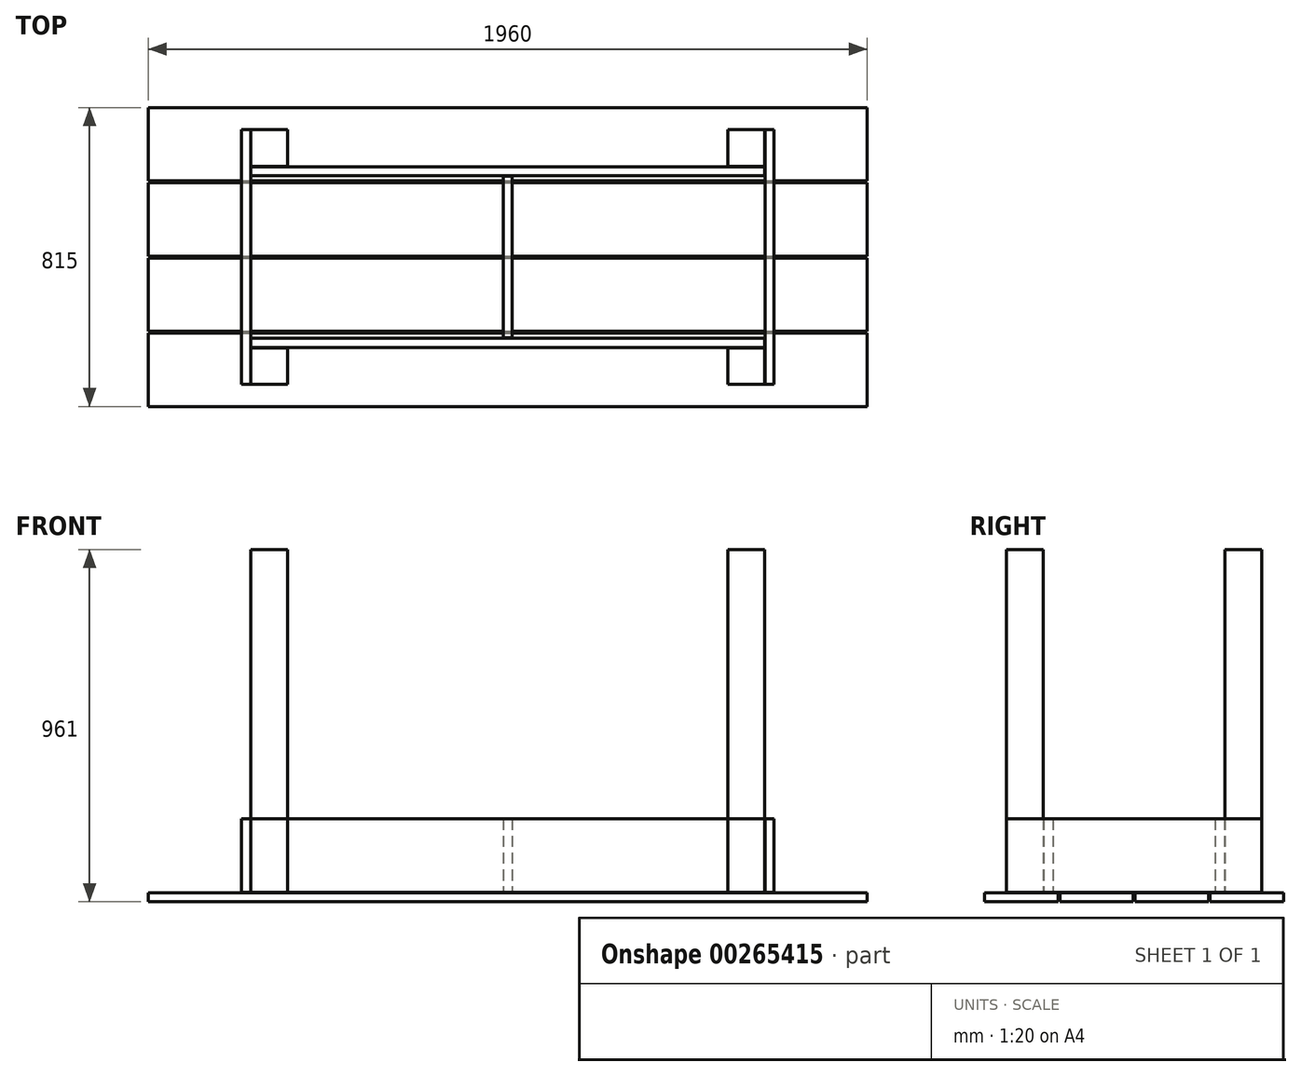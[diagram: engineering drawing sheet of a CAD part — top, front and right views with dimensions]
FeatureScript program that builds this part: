
annotation { "Feature Type Name" : "Feature", "Feature Type Description" : "" }
export const myFeature = defineFeature(function(context is Context, id is Id, definition is map)
    precondition{}
    {
        {
            var Q0;
            Q0=qCreatedBy(makeId("Top.planeOp"),FACE);
            var sketch = newSketch(context, id + "F0", { "sketchPlane" : qUnion([Q0])});
            skLineSegment(sketch, "E0.bottom", {"start": v(-916.06, -210.49) * mm, "end": v(1043.94, -210.49) * mm});
            skLineSegment(sketch, "E0.top", {"start": v(-916.06, -410.49) * mm, "end": v(1043.94, -410.49) * mm});
            skLineSegment(sketch, "E0.left", {"start": v(-916.06, -210.49) * mm, "end": v(-916.06, -410.49) * mm});
            skLineSegment(sketch, "E0.right", {"start": v(1043.94, -210.49) * mm, "end": v(1043.94, -410.49) * mm});
            skLineSegment(sketch, "E1.0.1.0", {"start": v(-916.06, -5.49) * mm, "end": v(-916.06, -205.49) * mm});
            skLineSegment(sketch, "E1.0.1.1", {"start": v(-916.06, -5.49) * mm, "end": v(1043.94, -5.49) * mm});
            skLineSegment(sketch, "E1.0.1.2", {"start": v(-916.06, -205.49) * mm, "end": v(1043.94, -205.49) * mm});
            skLineSegment(sketch, "E1.0.1.3", {"start": v(1043.94, -5.49) * mm, "end": v(1043.94, -205.49) * mm});
            skLineSegment(sketch, "E1.0.2.0", {"start": v(-916.06, 199.51) * mm, "end": v(-916.06, -0.49) * mm});
            skLineSegment(sketch, "E1.0.2.1", {"start": v(-916.06, 199.51) * mm, "end": v(1043.94, 199.51) * mm});
            skLineSegment(sketch, "E1.0.2.2", {"start": v(-916.06, -0.49) * mm, "end": v(1043.94, -0.49) * mm});
            skLineSegment(sketch, "E1.0.2.3", {"start": v(1043.94, 199.51) * mm, "end": v(1043.94, -0.49) * mm});
            skLineSegment(sketch, "E1.0.3.0", {"start": v(-916.06, 404.51) * mm, "end": v(-916.06, 204.51) * mm});
            skLineSegment(sketch, "E1.0.3.1", {"start": v(-916.06, 404.51) * mm, "end": v(1043.94, 404.51) * mm});
            skLineSegment(sketch, "E1.0.3.2", {"start": v(-916.06, 204.51) * mm, "end": v(1043.94, 204.51) * mm});
            skLineSegment(sketch, "E1.0.3.3", {"start": v(1043.94, 404.51) * mm, "end": v(1043.94, 204.51) * mm});
            skLineSegment(sketch, "E1.direction1", {"start": v(-916.06, -410.49) * mm, "end": v(-891.06, -410.49) * mm, "construction": true});
            skLineSegment(sketch, "E1.direction2", {"start": v(-916.06, -410.49) * mm, "end": v(-916.06, -205.49) * mm, "construction": true});
            skSolve(sketch);
        }
        {
            var Q0;
            Q0 = qSketchRegion(id + "F0", true);
            extrude(context, id + "F1", {"entities" : qUnion([Q0]), "depth" : 25 * mm});
        }
        {
            var Q0;
            Q0=makeQuery(id+"F1.opExtrude","CAP_FACE",FACE,{"disambiguationData":[OSD([sQuery(id+"F0.wireOp",EDGE,"E0.bottom"),sQuery(id+"F0.wireOp",EDGE,"E0.top"),sQuery(id+"F0.wireOp",EDGE,"E0.left"),sQuery(id+"F0.wireOp",EDGE,"E0.right")])],"isStart":false});
            cPlane(context, id + "F2", {"entities" : qUnion([Q0]), "cplaneType" : CPlaneType.OFFSET, "offset" : 1 * mm, "width" : 150 * mm, "height" : 150 * mm});
        }
        {
            var Q0;
            Q0=qCreatedBy(id+"F2.planeOp",FACE);
            var sketch = newSketch(context, id + "F3", { "sketchPlane" : qUnion([Q0])});
            skLineSegment(sketch, "E2.bottom", {"start": v(-916.06, 404.51) * mm, "end": v(1043.94, 404.51) * mm, "construction": true});
            skLineSegment(sketch, "E2.top", {"start": v(-916.06, -410.49) * mm, "end": v(1043.94, -410.49) * mm, "construction": true});
            skLineSegment(sketch, "E2.left", {"start": v(-916.06, 404.51) * mm, "end": v(-916.06, -410.49) * mm, "construction": true});
            skLineSegment(sketch, "E2.right", {"start": v(1043.94, 404.51) * mm, "end": v(1043.94, -410.49) * mm, "construction": true});
            skLineSegment(sketch, "E3", {"start": v(63.94, -410.49) * mm, "end": v(63.94, 404.51) * mm, "construction": true});
            skLineSegment(sketch, "E4", {"start": v(1043.94, -2.99) * mm, "end": v(-916.06, -2.99) * mm, "construction": true});
            skLineSegment(sketch, "E5.bottom", {"start": v(-636.06, 244.51) * mm, "end": v(-536.06, 244.51) * mm});
            skLineSegment(sketch, "E5.top", {"start": v(-636.06, 344.51) * mm, "end": v(-536.06, 344.51) * mm});
            skLineSegment(sketch, "E5.left", {"start": v(-636.06, 244.51) * mm, "end": v(-636.06, 344.51) * mm});
            skLineSegment(sketch, "E5.right", {"start": v(-536.06, 244.51) * mm, "end": v(-536.06, 344.51) * mm});
            skLineSegment(sketch, "E6.bottom", {"start": v(63.94, 218.51) * mm, "end": v(-636.06, 218.51) * mm});
            skLineSegment(sketch, "E6.top", {"start": v(63.94, 243.51) * mm, "end": v(-636.06, 243.51) * mm});
            skLineSegment(sketch, "E6.left", {"start": v(63.94, 218.51) * mm, "end": v(63.94, 243.51) * mm});
            skLineSegment(sketch, "E6.right", {"start": v(-636.06, 218.51) * mm, "end": v(-636.06, 243.51) * mm});
            skLineSegment(sketch, "E7.bottom", {"start": v(-662.06, -2.99) * mm, "end": v(-637.06, -2.99) * mm});
            skLineSegment(sketch, "E7.top", {"start": v(-662.06, 344.51) * mm, "end": v(-637.06, 344.51) * mm});
            skLineSegment(sketch, "E7.left", {"start": v(-662.06, -2.99) * mm, "end": v(-662.06, 344.51) * mm});
            skLineSegment(sketch, "E7.right", {"start": v(-637.06, -2.99) * mm, "end": v(-637.06, 344.51) * mm});
            skLineSegment(sketch, "E8.bottom", {"start": v(63.94, -2.99) * mm, "end": v(51.44, -2.99) * mm});
            skLineSegment(sketch, "E8.top", {"start": v(63.94, 217.51) * mm, "end": v(51.44, 217.51) * mm});
            skLineSegment(sketch, "E8.left", {"start": v(63.94, -2.99) * mm, "end": v(63.94, 217.51) * mm});
            skLineSegment(sketch, "E8.right", {"start": v(51.44, -2.99) * mm, "end": v(51.44, 217.51) * mm});
            skLineSegment(sketch, "E9.MirrorCS", {"start": v(763.94, 218.51) * mm, "end": v(763.94, 243.51) * mm});
            skLineSegment(sketch, "E10.MirrorCS", {"start": v(789.94, -2.99) * mm, "end": v(764.94, -2.99) * mm});
            skLineSegment(sketch, "E11.MirrorCS", {"start": v(789.94, 344.51) * mm, "end": v(764.94, 344.51) * mm});
            skLineSegment(sketch, "E12.MirrorCS", {"start": v(63.94, -2.99) * mm, "end": v(76.44, -2.99) * mm});
            skLineSegment(sketch, "E13.MirrorCS", {"start": v(63.94, 217.51) * mm, "end": v(76.44, 217.51) * mm});
            skLineSegment(sketch, "E14.MirrorCS", {"start": v(763.94, 244.51) * mm, "end": v(763.94, 344.51) * mm});
            skLineSegment(sketch, "E15.MirrorCS", {"start": v(763.94, 244.51) * mm, "end": v(663.94, 244.51) * mm});
            skLineSegment(sketch, "E16.MirrorCS", {"start": v(763.94, 344.51) * mm, "end": v(663.94, 344.51) * mm});
            skLineSegment(sketch, "E17.MirrorCS", {"start": v(663.94, 244.51) * mm, "end": v(663.94, 344.51) * mm});
            skLineSegment(sketch, "E18.MirrorCS", {"start": v(76.44, -2.99) * mm, "end": v(76.44, 217.51) * mm});
            skLineSegment(sketch, "E19.MirrorCS", {"start": v(764.94, -2.99) * mm, "end": v(764.94, 344.51) * mm});
            skLineSegment(sketch, "E20.MirrorCS", {"start": v(63.94, 243.51) * mm, "end": v(763.94, 243.51) * mm});
            skLineSegment(sketch, "E21.MirrorCS", {"start": v(63.94, 218.51) * mm, "end": v(763.94, 218.51) * mm});
            skLineSegment(sketch, "E22.MirrorCS", {"start": v(789.94, -2.99) * mm, "end": v(789.94, 344.51) * mm});
            skLineSegment(sketch, "E23.MirrorCS", {"start": v(63.94, -223.49) * mm, "end": v(76.44, -223.49) * mm});
            skLineSegment(sketch, "E24.MirrorCS", {"start": v(63.94, -223.49) * mm, "end": v(51.44, -223.49) * mm});
            skLineSegment(sketch, "E25.MirrorCS", {"start": v(63.94, -224.49) * mm, "end": v(63.94, -249.49) * mm});
            skLineSegment(sketch, "E26.MirrorCS", {"start": v(763.94, -224.49) * mm, "end": v(763.94, -249.49) * mm});
            skLineSegment(sketch, "E27.MirrorCS", {"start": v(789.94, -350.49) * mm, "end": v(764.94, -350.49) * mm});
            skLineSegment(sketch, "E28.MirrorCS", {"start": v(-636.06, -224.49) * mm, "end": v(-636.06, -249.49) * mm});
            skLineSegment(sketch, "E29.MirrorCS", {"start": v(-662.06, -350.49) * mm, "end": v(-637.06, -350.49) * mm});
            skLineSegment(sketch, "E30.MirrorCS", {"start": v(63.94, -2.99) * mm, "end": v(63.94, -223.49) * mm});
            skLineSegment(sketch, "E31.MirrorCS", {"start": v(-636.06, -250.49) * mm, "end": v(-536.06, -250.49) * mm});
            skLineSegment(sketch, "E32.MirrorCS", {"start": v(-662.06, -2.99) * mm, "end": v(-662.06, -350.49) * mm});
            skLineSegment(sketch, "E33.MirrorCS", {"start": v(763.94, -250.49) * mm, "end": v(663.94, -250.49) * mm});
            skLineSegment(sketch, "E34.MirrorCS", {"start": v(63.94, -224.49) * mm, "end": v(763.94, -224.49) * mm});
            skLineSegment(sketch, "E35.MirrorCS", {"start": v(76.44, -2.99) * mm, "end": v(76.44, -223.49) * mm});
            skLineSegment(sketch, "E36.MirrorCS", {"start": v(-636.06, -350.49) * mm, "end": v(-536.06, -350.49) * mm});
            skLineSegment(sketch, "E37.MirrorCS", {"start": v(63.94, -249.49) * mm, "end": v(-636.06, -249.49) * mm});
            skLineSegment(sketch, "E38.MirrorCS", {"start": v(-536.06, -250.49) * mm, "end": v(-536.06, -350.49) * mm});
            skLineSegment(sketch, "E39.MirrorCS", {"start": v(663.94, -250.49) * mm, "end": v(663.94, -350.49) * mm});
            skLineSegment(sketch, "E40.MirrorCS", {"start": v(63.94, -224.49) * mm, "end": v(-636.06, -224.49) * mm});
            skLineSegment(sketch, "E41.MirrorCS", {"start": v(51.44, -2.99) * mm, "end": v(51.44, -223.49) * mm});
            skLineSegment(sketch, "E42.MirrorCS", {"start": v(-636.06, -250.49) * mm, "end": v(-636.06, -350.49) * mm});
            skLineSegment(sketch, "E43.MirrorCS", {"start": v(764.94, -2.99) * mm, "end": v(764.94, -350.49) * mm});
            skLineSegment(sketch, "E44.MirrorCS", {"start": v(63.94, -249.49) * mm, "end": v(763.94, -249.49) * mm});
            skLineSegment(sketch, "E45.MirrorCS", {"start": v(763.94, -250.49) * mm, "end": v(763.94, -350.49) * mm});
            skLineSegment(sketch, "E46.MirrorCS", {"start": v(789.94, -2.99) * mm, "end": v(789.94, -350.49) * mm});
            skLineSegment(sketch, "E47.MirrorCS", {"start": v(763.94, -350.49) * mm, "end": v(663.94, -350.49) * mm});
            skLineSegment(sketch, "E48.MirrorCS", {"start": v(-637.06, -2.99) * mm, "end": v(-637.06, -350.49) * mm});
            skSolve(sketch);
        }
        {
            var Q0;
            Q0 = qSketchRegion(id + "F3", true);
            extrude(context, id + "F4", {"entities" : qUnion([Q0]), "depth" : 200 * mm});
        }
        {
            var Q0;
            Q0=makeQuery(id+"F4.opExtrude","CAP_FACE",FACE,{"disambiguationData":[OSD([sQuery(id+"F3.wireOp",EDGE,"E31.MirrorCS"),sQuery(id+"F3.wireOp",EDGE,"E36.MirrorCS"),sQuery(id+"F3.wireOp",EDGE,"E38.MirrorCS"),sQuery(id+"F3.wireOp",EDGE,"E42.MirrorCS")])],"isStart":false});
            var Q1;
            Q1=makeQuery(id+"F4.opExtrude","CAP_FACE",FACE,{"disambiguationData":[OSD([sQuery(id+"F3.wireOp",EDGE,"E5.bottom"),sQuery(id+"F3.wireOp",EDGE,"E5.top"),sQuery(id+"F3.wireOp",EDGE,"E5.left"),sQuery(id+"F3.wireOp",EDGE,"E5.right")])],"isStart":false});
            var Q2;
            Q2=makeQuery(id+"F4.opExtrude","CAP_FACE",FACE,{"disambiguationData":[OSD([sQuery(id+"F3.wireOp",EDGE,"E14.MirrorCS"),sQuery(id+"F3.wireOp",EDGE,"E15.MirrorCS"),sQuery(id+"F3.wireOp",EDGE,"E16.MirrorCS"),sQuery(id+"F3.wireOp",EDGE,"E17.MirrorCS")])],"isStart":false});
            var Q3;
            Q3=makeQuery(id+"F4.opExtrude","CAP_FACE",FACE,{"disambiguationData":[OSD([sQuery(id+"F3.wireOp",EDGE,"E33.MirrorCS"),sQuery(id+"F3.wireOp",EDGE,"E39.MirrorCS"),sQuery(id+"F3.wireOp",EDGE,"E45.MirrorCS"),sQuery(id+"F3.wireOp",EDGE,"E47.MirrorCS")])],"isStart":false});
            extrude(context, id + "F5", {"entities" : qUnion([Q0, Q1, Q2, Q3]), "depth" : 735 * mm});
        }
    });
